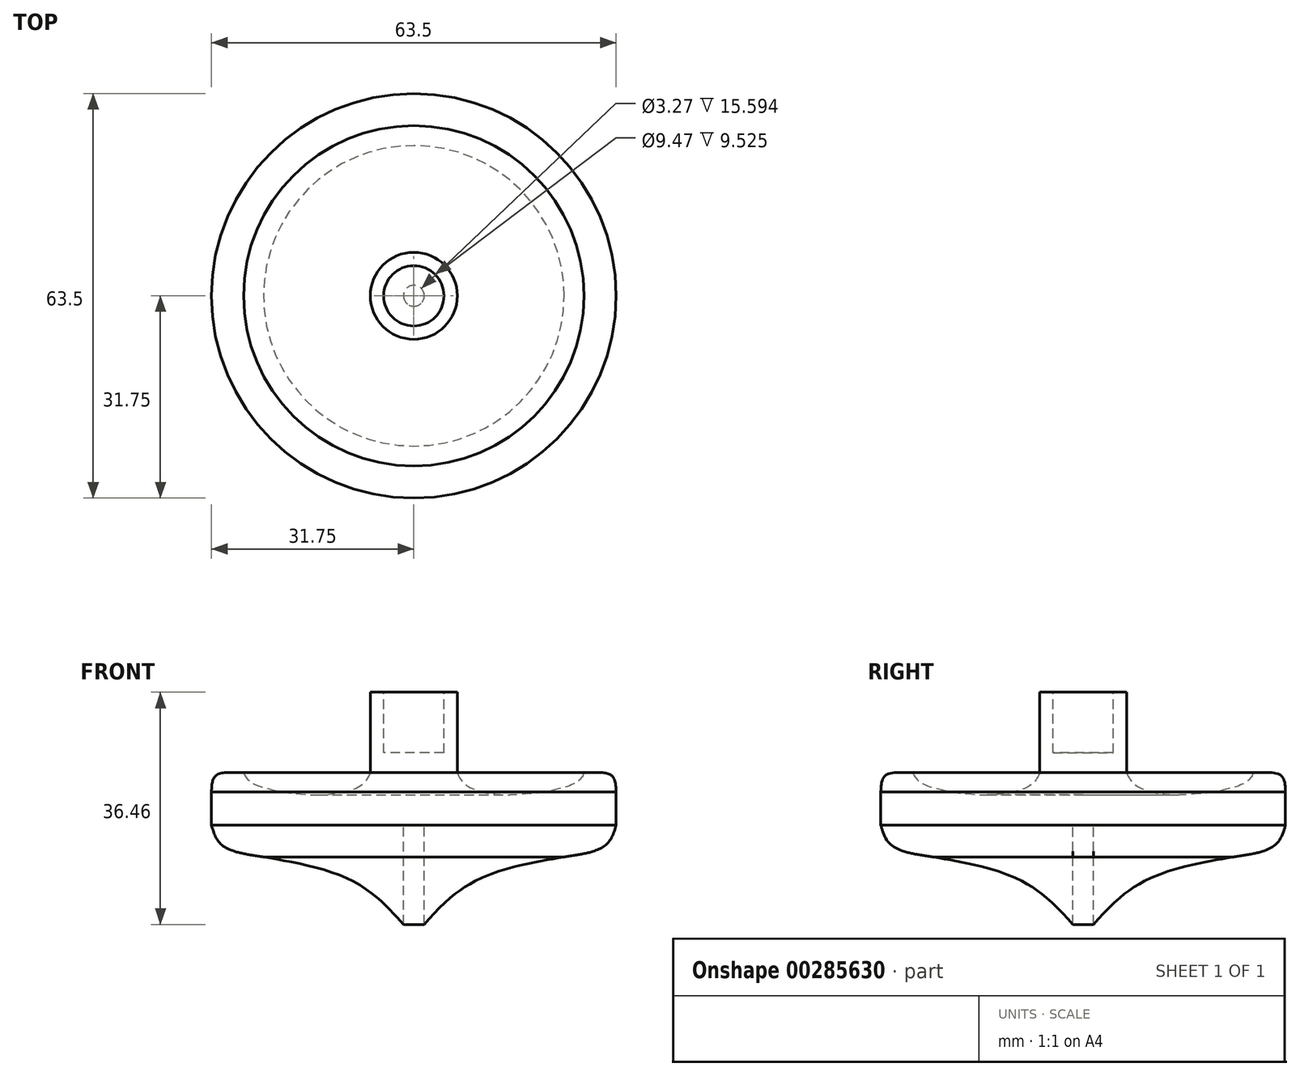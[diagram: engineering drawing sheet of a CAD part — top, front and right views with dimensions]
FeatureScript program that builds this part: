
annotation { "Feature Type Name" : "Feature", "Feature Type Description" : "" }
export const myFeature = defineFeature(function(context is Context, id is Id, definition is map)
    precondition{}
    {
        {
            var Q0;
            Q0=qCreatedBy(makeId("Front.planeOp"),FACE);
            var sketch = newSketch(context, id + "F0", { "sketchPlane" : qUnion([Q0])});
            skLineSegment(sketch, "E0", {"start": v(0, 8.17) * mm, "end": v(0, 0) * mm});
            skLineSegment(sketch, "E1.MirrorCS", {"start": v(0, 0) * mm, "end": v(-31.75, 0) * mm});
            skPoint(sketch, "E2", {"position": v(-26.72, 8.17) * mm});
            skPoint(sketch, "E3", {"position": v(-26.72, 4.48) * mm});
            skLineSegment(sketch, "E4", {"start": v(-26.72, 8.17) * mm, "end": v(-26.72, 4.48) * mm});
            skLineSegment(sketch, "E5", {"start": v(-26.72, 4.48) * mm, "end": v(0, 4.48) * mm});
            skPoint(sketch, "E5.endSnap0", {"position": v(0, 4.09) * mm});
            skLineSegment(sketch, "E6", {"start": v(0, 4.48) * mm, "end": v(0, 8.17) * mm});
            skPoint(sketch, "E7.orphan", {"position": v(0, 8.17) * mm});
            skPoint(sketch, "E8.MirrorCS.start.orphan", {"position": v(-6.83, 8.17) * mm});
            skPoint(sketch, "E9.MirrorCS.start.orphan", {"position": v(-6.83, 4.48) * mm});
            skLineSegment(sketch, "E10.MirrorCS", {"start": v(-6.83, 8.17) * mm, "end": v(-4.76, 8.17) * mm});
            skLineSegment(sketch, "E11.MirrorCS", {"start": v(-6.83, 4.48) * mm, "end": v(-6.83, 8.17) * mm});
            skLineSegment(sketch, "E12", {"start": v(1.57, 0) * mm, "end": v(1.62, 0) * mm});
            skPoint(sketch, "E13", {"position": v(1.58, -14.3) * mm});
            skPoint(sketch, "E14", {"position": v(0, -14.3) * mm});
            skLineSegment(sketch, "E15", {"start": v(0, -4.12) * mm, "end": v(0, 0) * mm});
            skLineSegment(sketch, "E16", {"start": v(0, -4.12) * mm, "end": v(0, -17.56) * mm});
            skLineSegment(sketch, "E17", {"start": v(0, 8.17) * mm, "end": v(-6.83, 8.17) * mm});
            skFitSpline(sketch, "E18", {"points": [v(-31.75, 0) * mm, v(-30.07, -3.16) * mm, v(-23.59, -4.99) * mm], "startDerivative": vector(2.47, -8.4) * mm, "endDerivative": vector(13.29, -1.92) * mm});
            skLineSegment(sketch, "E19", {"start": v(-28.1, -4.12) * mm, "end": v(0, -4.12) * mm});
            skFitSpline(sketch, "E20", {"points": [v(-28.1, -4.12) * mm, v(-23.59, -4.99) * mm, v(-10.47, -8.36) * mm, v(-3, -14.06) * mm, v(0, -17.56) * mm], "startDerivative": vector(19.43, -4) * mm, "endDerivative": vector(13.85, -16.93) * mm});
            skFitSpline(sketch, "E21", {"points": [v(-26.72, 8.17) * mm, v(-26.33, 7.53) * mm, v(-24.89, 6.38) * mm, v(-14.44, 4.76) * mm, v(-8.12, 6.38) * mm, v(-6.83, 8.17) * mm], "startDerivative": vector(3.72, -6.89) * mm, "endDerivative": vector(5.92, 12.1) * mm});
            skFitSpline(sketch, "E22", {"points": [v(-26.72, 8.17) * mm, v(-31.07, 7.78) * mm, v(-31.75, 5.24) * mm], "startDerivative": vector(-9.45, 0.73) * mm, "endDerivative": vector(-0.22, -6.92) * mm});
            skLineSegment(sketch, "E23", {"start": v(-31.75, 5.24) * mm, "end": v(-31.75, 0) * mm});
            skSolve(sketch);
        }
        {
            var Q0;
            Q0=qSketchRegion(id+"F0",true);
            var Q1;
            Q1=sQuery(id+"F0.wireOp",EDGE,"E15");
            revolve(context, id + "F1", {"entities" : qUnion([Q0]), "axis" : qUnion([Q1]), "revolveType" : RevolveType.FULL});
        }
        {
            var Q0;
            Q0=makeQuery(id+"FKuZFqlpUha3mlx_1.boolean.opBoolean","COPY",FACE,{"derivedFrom":makeQuery(id+"FKuZFqlpUha3mlx_1.opExtrude","CAP_FACE",FACE,{"disambiguationData":[OSD([sQuery(id+"F9vJmQ9T3XhcaWq_1.wireOp",EDGE,"lq9LEbIw-argm-Qz1Q-cuVm-DKIxFWfjvfAz")])],"isStart":true})});
            var Q1;
            Q1=makeQuery(id+"F1.opRevolve","SWEPT_FACE",FACE,{"disambiguationData":[OSD([sQuery(id+"F0.wireOp",EDGE,"E17")])]});
            extrude(context, id + "F2", {"entities" : qUnion([Q0, Q1]), "operationType" : NewBodyOperationType.ADD, "depth" : 12.7 * mm});
        }
        {
            var Q0;
            Q0=qCreatedBy(makeId("Top.planeOp"),FACE);
            var sketch = newSketch(context, id + "F3", { "sketchPlane" : qUnion([Q0])});
            skCircle(sketch, "E24", {"center": v(0, 0) * mm, "radius": 1.63 * mm});
            skSolve(sketch);
        }
        {
            var Q0;
            Q0=qSketchRegion(id+"F3",true);
            extrude(context, id + "F4", {"entities" : qUnion([Q0]), "operationType" : NewBodyOperationType.REMOVE, "oppositeDirection" : true, "depth" : 19.66 * mm});
        }
        {
            var Q0;
            Q0=makeQuery(id+"F2.opExtrude","CAP_FACE",FACE,{"disambiguationData":[OSD([sQuery(id+"F0.wireOp",EDGE,"E17")])],"isStart":false});
            var sketch = newSketch(context, id + "F5", { "sketchPlane" : qUnion([Q0])});
            skCircle(sketch, "E25", {"center": v(0, 0) * mm, "radius": 4.73 * mm});
            skSolve(sketch);
        }
        {
            var Q0;
            Q0=makeQuery(id+"F5.imprint","IMPRINT",FACE,{"disambiguationData":[TD([[makeQuery(id+"F5.imprint","IMPRINT",EDGE,{"derivedFrom":sQuery(id+"F5.wireOp",EDGE,"E25")}),1.0]])]});
            var Q1;
            Q1=sQuery(id+"F5.wireOp",EDGE,"E25");
            extrude(context, id + "F6", {"entities" : qUnion([Q0]), "operationType" : NewBodyOperationType.REMOVE, "surfaceEntities" : qUnion([Q1]), "oppositeDirection" : true, "depth" : 9.52 * mm});
        }
    });
